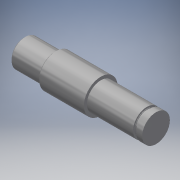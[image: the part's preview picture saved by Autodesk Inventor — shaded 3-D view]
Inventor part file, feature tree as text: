
AUTODESK INVENTOR PART (.ipt)
format: ipt  version: 2019 (Build 230136000, 136)  size: 143,872 bytes
history: native  units: mm
features: other x6, chamfer x2
ambient origin geometry x6: Origin, XZ Plane, XY Plane, X Axis, Y Axis, Z Axis
bodies: Body1 (feature_tree)
feature tree (8):
  other  "實體1"
  other  "迴轉1"
  other  "扣環槽3"
  chamfer  "倒角2"  [1 undecoded]
  chamfer  "倒角1"  Distance=9.0mm
  other  "起始平面"
  other  "主要草圖"
  other  "iFeature27:3"
note: 1 required parameter value undecoded (feature->parameter linkage not recoverable at this tier; creation-order binding heuristic only, values carry confidence <= 0.55)
